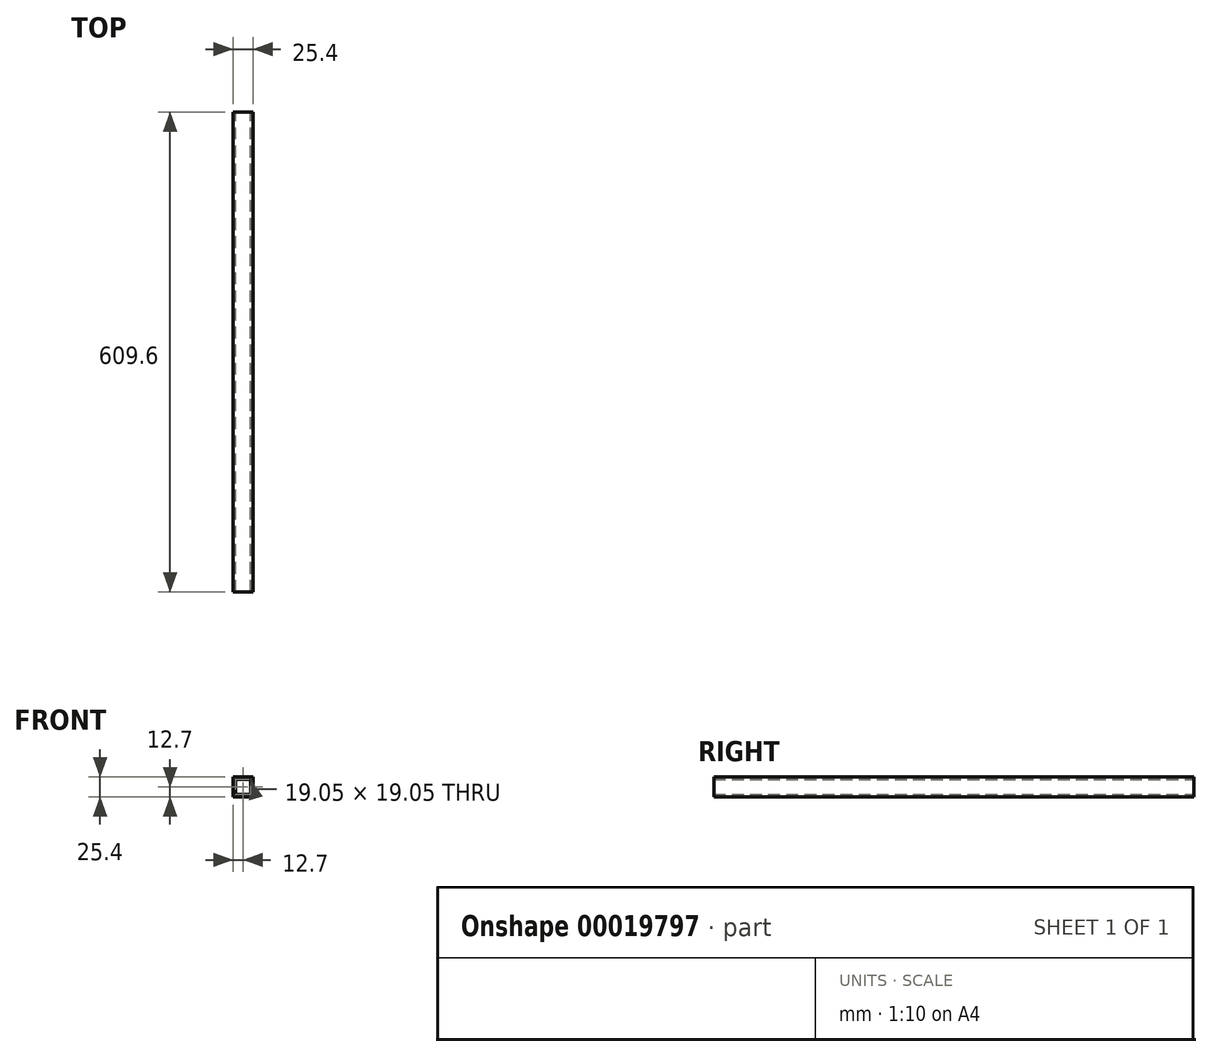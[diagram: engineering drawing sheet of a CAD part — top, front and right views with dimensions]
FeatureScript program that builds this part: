
annotation { "Feature Type Name" : "Feature", "Feature Type Description" : "" }
export const myFeature = defineFeature(function(context is Context, id is Id, definition is map)
    precondition{}
    {
        {
            var Q0;
            Q0=qCreatedBy(makeId("Front.planeOp"),FACE);
            var sketch = newSketch(context, id + "F0", { "sketchPlane" : qUnion([Q0])});
            skLineSegment(sketch, "E0.rect.bottom", {"start": v(12.7, 12.7) * mm, "end": v(-12.7, 12.7) * mm});
            skLineSegment(sketch, "E0.rect.top", {"start": v(12.7, -12.7) * mm, "end": v(-12.7, -12.7) * mm});
            skLineSegment(sketch, "E0.rect.left", {"start": v(12.7, 12.7) * mm, "end": v(12.7, -12.7) * mm});
            skLineSegment(sketch, "E0.rect.right", {"start": v(-12.7, 12.7) * mm, "end": v(-12.7, -12.7) * mm});
            skPoint(sketch, "E0.rect.middle", {"position": v(0, 0) * mm});
            skLineSegment(sketch, "E1.rect.bottom", {"start": v(9.52, 9.53) * mm, "end": v(-9.53, 9.53) * mm});
            skLineSegment(sketch, "E1.rect.top", {"start": v(9.53, -9.53) * mm, "end": v(-9.52, -9.53) * mm});
            skLineSegment(sketch, "E1.rect.left", {"start": v(9.53, 9.53) * mm, "end": v(9.53, -9.53) * mm});
            skLineSegment(sketch, "E1.rect.right", {"start": v(-9.53, 9.53) * mm, "end": v(-9.52, -9.53) * mm});
            skSolve(sketch);
        }
        {
            var Q0;
            Q0=makeQuery(id+"F0.imprint","IMPRINT",FACE,{"disambiguationData":[TD([[makeQuery(id+"F0.imprint","IMPRINT",EDGE,{"derivedFrom":sQuery(id+"F0.wireOp",EDGE,"E0.rect.bottom")}),1.0]])]});
            extrude(context, id + "F1", {"entities" : qUnion([Q0]), "endBound" : BoundingType.SYMMETRIC, "depth" : 609.6 * mm});
        }
    });
